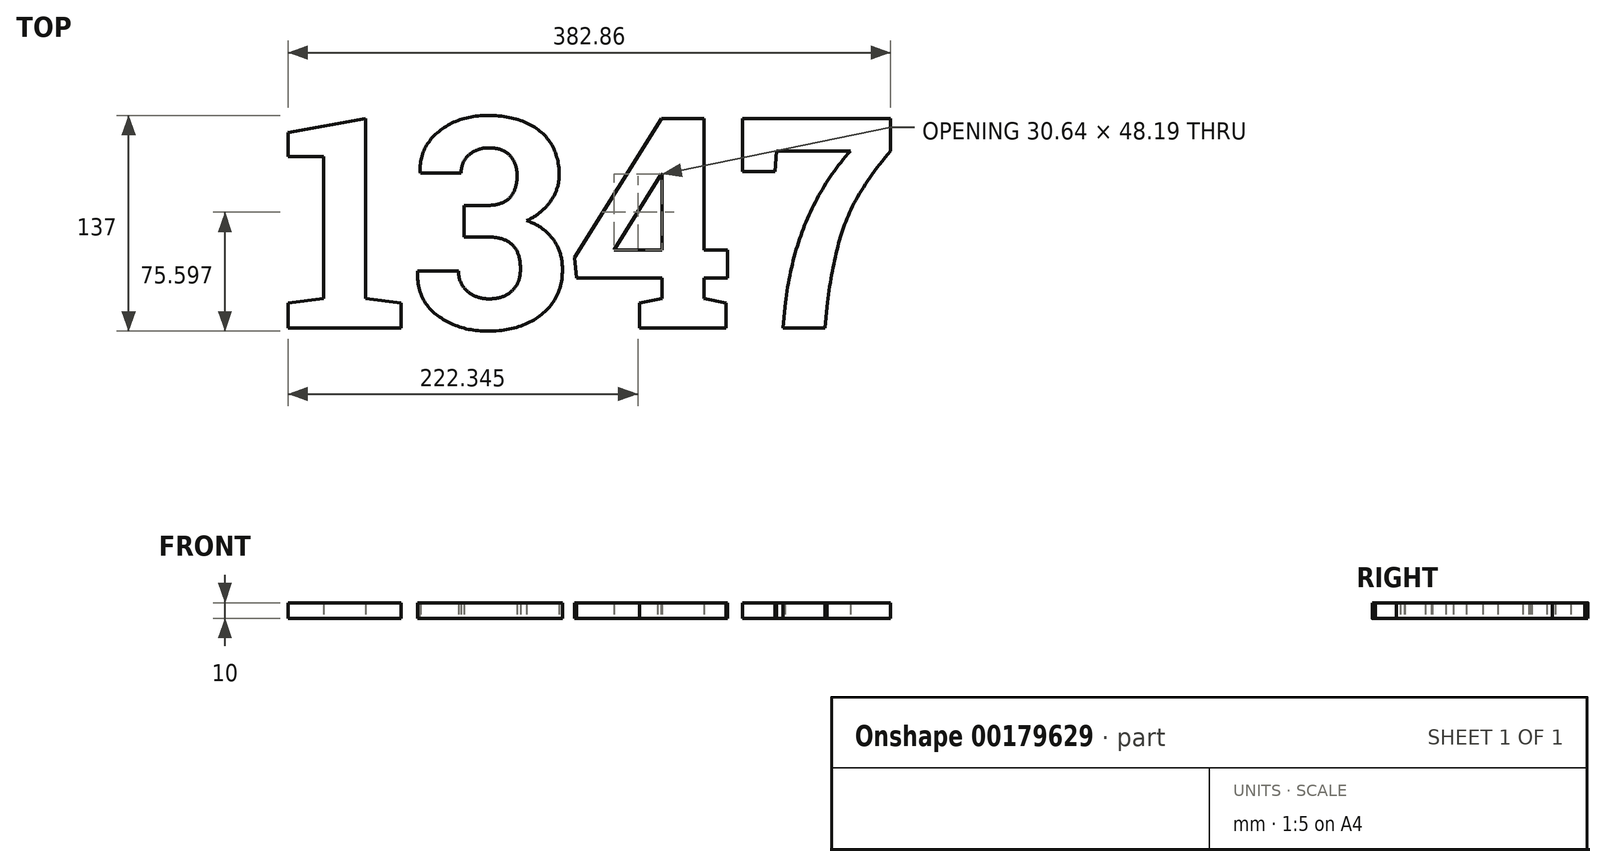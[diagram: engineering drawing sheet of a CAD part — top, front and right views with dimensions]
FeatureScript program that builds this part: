
annotation { "Feature Type Name" : "Feature", "Feature Type Description" : "" }
export const myFeature = defineFeature(function(context is Context, id is Id, definition is map)
    precondition{}
    {
        {
            var Q0;
            Q0=qCreatedBy(makeId("Top.planeOp"),FACE);
            var sketch = newSketch(context, id + "F0", { "sketchPlane" : qUnion([Q0])});
            skText(sketch, "E0", { "text": "1347", "fontName": "RobotoSlab-Bold.ttf"});
            const initialGuessF0  = {"E0": [-0.2, -0.06742, 1, 0, 0.13484]};
            skSetInitialGuess(sketch, initialGuessF0);
            skSolve(sketch);
        }
        {
            var Q0;
            Q0 = qSketchRegion(id + "F0", true);
            extrude(context, id + "F1", {"entities" : qUnion([Q0]), "depth" : 10 * mm});
        }
    });
